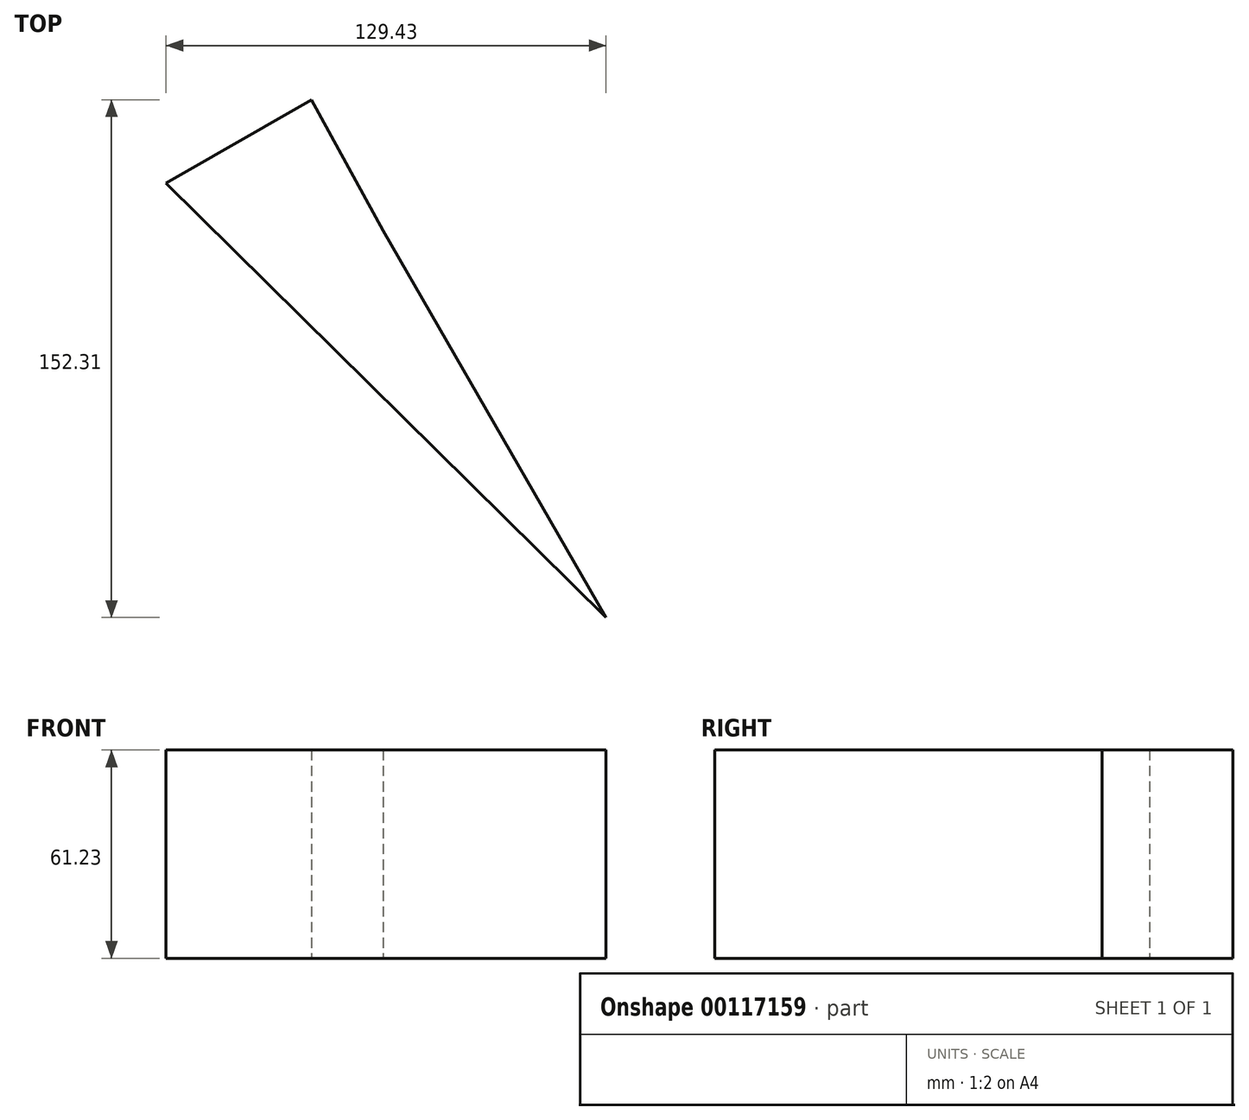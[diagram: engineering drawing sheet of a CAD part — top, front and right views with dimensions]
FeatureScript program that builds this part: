
annotation { "Feature Type Name" : "Feature", "Feature Type Description" : "" }
export const myFeature = defineFeature(function(context is Context, id is Id, definition is map)
    precondition{}
    {
        {
            var Q0;
            Q0=qCreatedBy(makeId("Top.planeOp"),FACE);
            var sketch = newSketch(context, id + "F0", { "sketchPlane" : qUnion([Q0])});
            skLineSegment(sketch, "E0", {"start": v(-126.17, -70.72) * mm, "end": v(-255.6, 57.13) * mm});
            skLineSegment(sketch, "E1", {"start": v(-255.6, 57.13) * mm, "end": v(-212.81, 81.6) * mm});
            skLineSegment(sketch, "E2", {"start": v(-212.81, 81.6) * mm, "end": v(-191.7, 43.14) * mm});
            skLineSegment(sketch, "E3", {"start": v(-191.7, 43.14) * mm, "end": v(-126.17, -70.72) * mm});
            skSolve(sketch);
        }
        {
            var Q0;
            Q0 = qSketchRegion(id + "F0", true);
            extrude(context, id + "F1", {"entities" : qUnion([Q0]), "depth" : 61.23 * mm});
        }
    });
